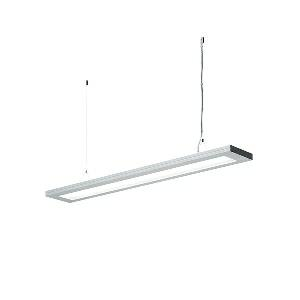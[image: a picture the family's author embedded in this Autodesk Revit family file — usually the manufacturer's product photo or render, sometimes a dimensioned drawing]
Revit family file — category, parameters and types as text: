
# Revit family: lavigo_-_dpp_480_d_vtl_00679837_4465
name_source: partatom
category: Lighting Fixtures
units: mm (PartAtom-declared; Revit-internal decimal feet)

## family parameters
Cut with Voids When Loaded = No
Host = Face
Light Source = No
Part Type = Normal
Room Calculation Point = No
Round Connector Dimension = Use Diameter
Shared = No

## types (1)
- LAVIGO - DPP 480/D VTL (1 x LED VTL, 5450 lm, 3000-6500K)
    Apparent Load = 42 VA
    Approval mark = CE
    CIE Flux Codes = 66 91 98 19 100
    Color Rendering = 80-89
    Color Temperature = 3000-6500K
    Control Gear = Electronic ballast
    Default Elevation = 1800 mm
    Description = DPP 480/D|Suspended luminaire|light source: LED Daylight 3000-6500 K  Energy efficiency category A/A+/A++|  Daylight 4000 K 4000 K Energy efficiency category A++|connected load: 220-240 V, 50/60 Hz|Power consumption: approx. 42 W|standby: approx. 0,98|luminous flux: 5450 lm|luminous efficacy: 129 lm/W|light distribution: Direct/indirect|direct ratio: approx. 19 %|color rendering index (CRI): >= 80|chromaticity tolerance:  3 SDCM|System of protection: IP 20|technology: Continuously dimmable|luminaire body|material: Steel/plastic|surface: Painted|colour: White|lamp cover: Polycarbonate (PC), Clear|mains lead: 1.00 m With free stranded wires|Fastening: Steel cable 0.3 - 0.7 m|decorative contrast side parts: Flint grey|glare control: Prism aperture|luminance(L65): <= 1200 cd/m|unified glare rating(4H 8H): <=  16|special features: Specified values at approx. 4000 K, DALI - dimming via digital rotary dimmer, DALI Load 2x, Integration into DALI light management system for biodynamic light VTL, Light forming, Separated, direct and indirect light individually adjustable|
    Frequency = 50 Hz
    Height = 36 mm
    Lamp = 1 x LED VTL
    Lamp Light Flux = 5450 lm
    Lamp count = 1
    Length = 1245 mm
    Luminous efficacy = 130 lm/W
    Manufacturer = Waldmann
    ModVariant = No
    Model = 00679837
    Mounting Place = Ceiling
    Mounting Type = Pendant
    Number of Poles = 1
    OnlyDefault = Yes
    Power Factor = 1
    Product Name = LAVIGO - DPP 480/D VTL
    Product group = Suspended luminaire
    ProductGroupID = 9
    Protection Class = Protection class I
    Protection Degree = IP 20
    RLX_Detail_Level = 1
    RLX_Emergency_Light_Flux = 0 lm
    RLX_Emergency_Type = 0
    RLX_Emergency_Type_DB = No
    RlxData = <blob elided: 24845 chars, md5=77a82239>
    Socket = socket
    Standby Power = 0 W
    System Light Flux = 5450 lm
    System Power = 42 W
    Type Comments = Product without accessories
    Type Image = 121740000-00678744.jpg
    URL = http://relux.com
    VarID = ---
    Voltage = 230 V
    Voltage Range = 220-240 V
    Weight = 0.00 kg
    Width = 200 mm

## geometry (parser evidence)
native form markers: Blend x4, Sweep x13
no freeform markers — native parametric forms only
